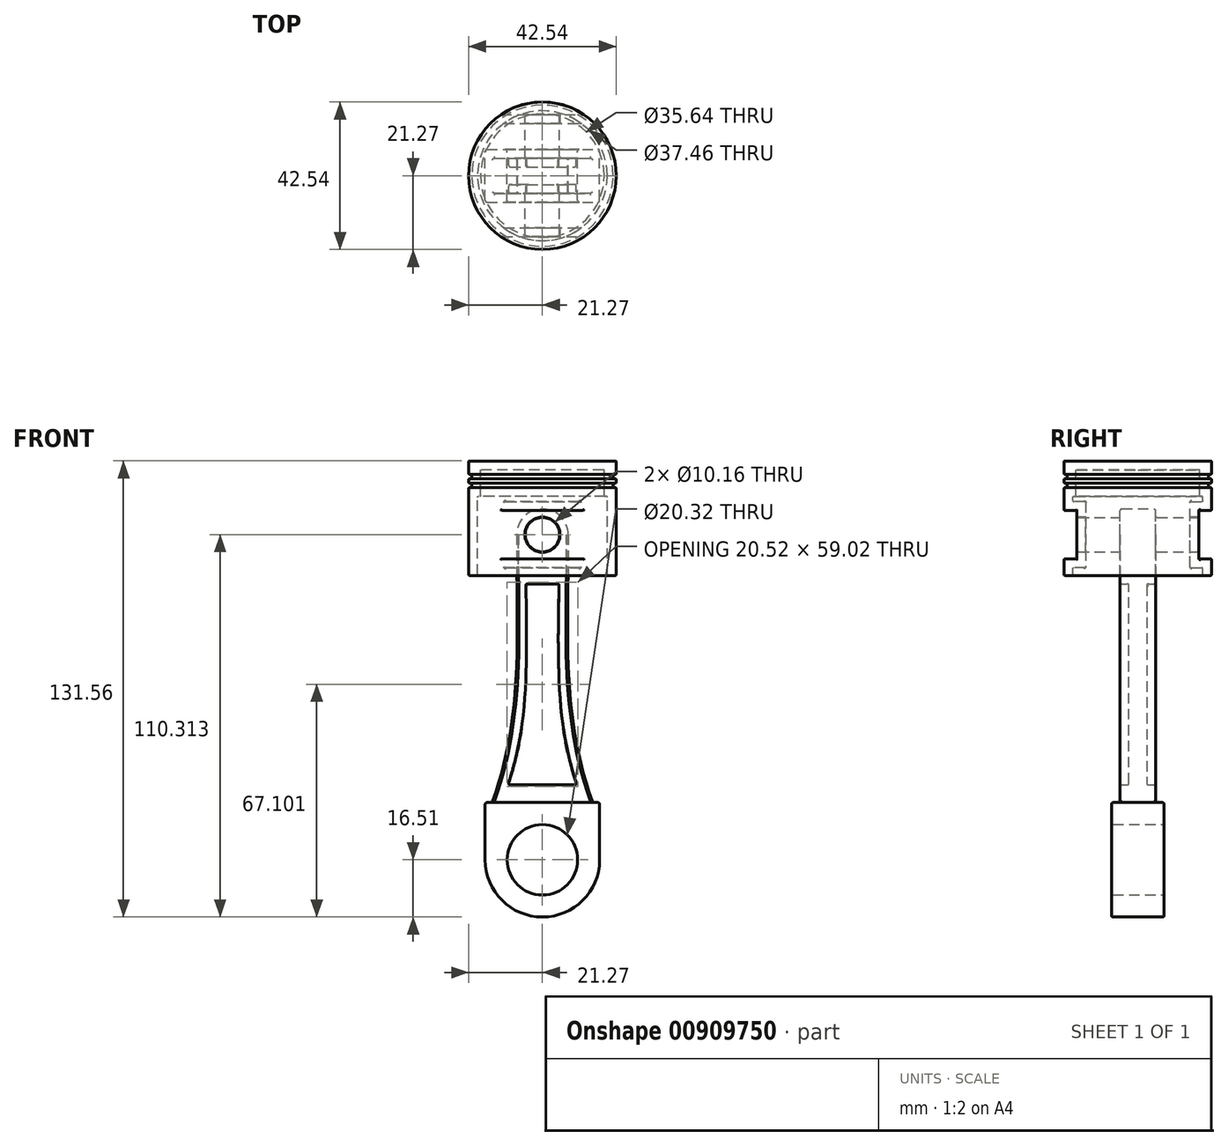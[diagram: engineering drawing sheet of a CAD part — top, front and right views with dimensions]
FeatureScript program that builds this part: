
annotation { "Feature Type Name" : "Feature", "Feature Type Description" : "" }
export const myFeature = defineFeature(function(context is Context, id is Id, definition is map)
    precondition{}
    {
        {
            var Q0;
            Q0=qCreatedBy(makeId("Front.planeOp"),FACE);
            var sketch = newSketch(context, id + "F0", { "sketchPlane" : qUnion([Q0])});
            skLineSegment(sketch, "E0", {"start": v(-248.97, 187.24) * mm, "end": v(-248.97, -66.76) * mm});
            skLineSegment(sketch, "E1", {"start": v(221.96, 188.73) * mm, "end": v(289.05, 188.73) * mm});
            skSolve(sketch);
        }
        {
            var Q0;
            Q0=qCreatedBy(makeId("Front.planeOp"),FACE);
            var sketch = newSketch(context, id + "F1", { "sketchPlane" : qUnion([Q0])});
            skLineSegment(sketch, "E2.bottom", {"start": v(0, 115.05) * mm, "end": v(21.27, 115.05) * mm});
            skLineSegment(sketch, "E2.top", {"start": v(0, 82.03) * mm, "end": v(21.27, 82.03) * mm});
            skLineSegment(sketch, "E2.left", {"start": v(0, 115.05) * mm, "end": v(0, 111.17) * mm});
            skLineSegment(sketch, "E2.right", {"start": v(21.27, 115.05) * mm, "end": v(21.27, 111.17) * mm});
            skLineSegment(sketch, "E3.left", {"start": v(0, 111.17) * mm, "end": v(0, 109.9) * mm});
            skLineSegment(sketch, "E3.right", {"start": v(20.36, 111.17) * mm, "end": v(20.36, 109.9) * mm});
            skLineSegment(sketch, "E4.left", {"start": v(20.36, 108.63) * mm, "end": v(20.36, 107.36) * mm});
            skLineSegment(sketch, "E4.right", {"start": v(0, 108.63) * mm, "end": v(0, 107.36) * mm});
            skLineSegment(sketch, "E5", {"start": v(20.36, 111.17) * mm, "end": v(21.27, 111.17) * mm});
            skLineSegment(sketch, "E6", {"start": v(20.36, 109.9) * mm, "end": v(21.27, 109.9) * mm});
            skLineSegment(sketch, "E7", {"start": v(20.36, 108.63) * mm, "end": v(21.27, 108.63) * mm});
            skLineSegment(sketch, "E8", {"start": v(20.36, 107.36) * mm, "end": v(21.27, 107.36) * mm});
            skLineSegment(sketch, "E9.trimOffspring", {"start": v(21.27, 107.36) * mm, "end": v(21.27, 82.03) * mm});
            skLineSegment(sketch, "E10.trimOffspring", {"start": v(21.27, 109.9) * mm, "end": v(21.27, 108.63) * mm});
            skLineSegment(sketch, "E11.trimOffspring", {"start": v(0, 109.9) * mm, "end": v(0, 108.63) * mm});
            skLineSegment(sketch, "E12.trimOffspring", {"start": v(0, 107.36) * mm, "end": v(0, 82.03) * mm});
            skSolve(sketch);
        }
        {
            var Q0;
            Q0 = qSketchRegion(id + "F1", true);
            var Q1;
            Q1=sQuery(id+"F1.wireOp",EDGE,"E12.trimOffspring");
            revolve(context, id + "F2", {"surfaceOperationType" : NewSurfaceOperationType.NEW, "entities" : qUnion([Q0]), "axis" : qUnion([Q1]), "revolveType" : RevolveType.FULL});
        }
        {
            var Q0;
            Q0=qCreatedBy(makeId("Right.planeOp"),FACE);
            var sketch = newSketch(context, id + "F3", { "sketchPlane" : qUnion([Q0])});
            skLineSegment(sketch, "E13.bottom", {"start": v(-21.43, 100.81) * mm, "end": v(-17.58, 100.81) * mm});
            skLineSegment(sketch, "E13.top", {"start": v(-21.43, 86.8) * mm, "end": v(-17.58, 86.8) * mm});
            skLineSegment(sketch, "E13.left", {"start": v(-21.43, 100.81) * mm, "end": v(-21.43, 86.8) * mm});
            skLineSegment(sketch, "E13.right", {"start": v(-17.58, 100.81) * mm, "end": v(-17.58, 86.8) * mm});
            skLineSegment(sketch, "E14.MirrorCS", {"start": v(17.58, 100.81) * mm, "end": v(17.58, 86.8) * mm});
            skLineSegment(sketch, "E15.MirrorCS", {"start": v(21.43, 100.81) * mm, "end": v(17.58, 100.81) * mm});
            skLineSegment(sketch, "E16.MirrorCS", {"start": v(21.43, 86.8) * mm, "end": v(17.58, 86.8) * mm});
            skLineSegment(sketch, "E17.MirrorCS", {"start": v(21.43, 100.81) * mm, "end": v(21.43, 86.8) * mm});
            skSolve(sketch);
        }
        {
            var Q0;
            Q0 = qSketchRegion(id + "F3", true);
            extrude(context, id + "F4", {"entities" : qUnion([Q0]), "operationType" : NewBodyOperationType.REMOVE, "oppositeDirection" : true, "depth" : 30.23 * mm, "offsetDistance" : 25.4 * mm, "hasSecondDirection" : true, "secondDirectionOppositeDirection" : false, "secondDirectionDepth" : 46.23 * mm});
        }
        {
            var Q0;
            Q0=makeQuery(id+"F2.opRevolve","SWEPT_FACE",FACE,{"disambiguationData":[OSD([sQuery(id+"F1.wireOp",EDGE,"E2.top")])]});
            shell(context, id + "F5", {"entities" : qUnion([Q0]), "thickness" : 2.54 * mm});
        }
        {
            var Q0;
            Q0=qCreatedBy(makeId("Front.planeOp"),FACE);
            var sketch = newSketch(context, id + "F6", { "sketchPlane" : qUnion([Q0])});
            skCircle(sketch, "E18", {"center": v(0, 93.8) * mm, "radius": 5.08 * mm});
            skSolve(sketch);
        }
        {
            var Q0;
            Q0 = qSketchRegion(id + "F6", true);
            extrude(context, id + "F7", {"entities" : qUnion([Q0]), "operationType" : NewBodyOperationType.REMOVE, "oppositeDirection" : true, "depth" : 25.4 * mm, "offsetDistance" : 25.4 * mm, "hasSecondDirection" : true, "secondDirectionOppositeDirection" : false, "secondDirectionDepth" : 25.4 * mm});
        }
        {
            var Q0;
            Q0=qCreatedBy(makeId("Front.planeOp"),FACE);
            var sketch = newSketch(context, id + "F8", { "sketchPlane" : qUnion([Q0])});
            skCircle(sketch, "E19", {"center": v(0, 0) * mm, "radius": 10.16 * mm});
            skArc(sketch, "E20", {"start": v(-16.51, 0) * mm, "mid": v(0, -16.51) * mm, "end": v(16.51, 0) * mm});
            skLineSegment(sketch, "E21.bottom", {"start": v(-16.51, 0) * mm, "end": v(16.51, 0) * mm});
            skLineSegment(sketch, "E21.top", {"start": v(-16.51, 16.51) * mm, "end": v(16.51, 16.51) * mm});
            skLineSegment(sketch, "E21.left", {"start": v(-16.51, 0) * mm, "end": v(-16.51, 16.51) * mm});
            skLineSegment(sketch, "E21.right", {"start": v(16.51, 0) * mm, "end": v(16.51, 16.51) * mm});
            skSolve(sketch);
        }
        {
            var Q0;
            Q0 = qSketchRegion(id + "F8", true);
            extrude(context, id + "F9", {"entities" : qUnion([Q0]), "depth" : 7.62 * mm, "offsetDistance" : 25.4 * mm, "hasSecondDirection" : true, "secondDirectionOppositeDirection" : true, "secondDirectionDepth" : 7.62 * mm});
        }
        {
            var Q0;
            Q0=qCreatedBy(makeId("Front.planeOp"),FACE);
            var sketch = newSketch(context, id + "F10", { "sketchPlane" : qUnion([Q0])});
            skFitSpline(sketch, "E22", {"points": [v(7.42, 93.84) * mm, v(14.48, 16.51) * mm], "startDerivative": vector(0.4, -85.18) * mm, "endDerivative": vector(27.69, -77.4) * mm});
            skLineSegment(sketch, "E23", {"start": v(0, 0) * mm, "end": v(0, 21.54) * mm});
            skFitSpline(sketch, "E24.MirrorCS", {"points": [v(-7.42, 93.84) * mm, v(-14.48, 16.51) * mm], "startDerivative": vector(-0.4, -85.18) * mm, "endDerivative": vector(-27.69, -77.4) * mm});
            skArc(sketch, "E25", {"start": v(-7.42, 93.84) * mm, "mid": v(0, 101.22) * mm, "end": v(7.42, 93.84) * mm});
            skFitSpline(sketch, "E26.0", {"points": [v(-4.88, 93.83) * mm, v(-4.91, 86.76) * mm, v(-4.68, 73.25) * mm, v(-4.71, 54.03) * mm, v(-6.49, 35.11) * mm, v(-9.73, 22.25) * mm, v(-12.1, 15.65) * mm]});
            skFitSpline(sketch, "E26.2", {"points": [v(4.88, 93.83) * mm, v(4.91, 86.76) * mm, v(4.68, 73.25) * mm, v(4.71, 54.03) * mm, v(6.49, 35.11) * mm, v(9.73, 22.25) * mm, v(12.1, 15.65) * mm]});
            skLineSegment(sketch, "E27", {"start": v(-4.8, 79.6) * mm, "end": v(4.8, 79.6) * mm});
            skLineSegment(sketch, "E28.trimOffspring", {"start": v(-10.15, 21.59) * mm, "end": v(10.15, 21.59) * mm});
            skLineSegment(sketch, "E29", {"start": v(-14.48, 16.51) * mm, "end": v(14.48, 16.51) * mm});
            skSolve(sketch);
        }
        {
            var Q0;
            Q0 = qSketchRegion(id + "F10", true);
            extrude(context, id + "F11", {"entities" : qUnion([Q0]), "operationType" : NewBodyOperationType.ADD, "depth" : 5.08 * mm, "offsetDistance" : 25.4 * mm, "hasSecondDirection" : true, "secondDirectionOppositeDirection" : true, "secondDirectionDepth" : 5.08 * mm});
        }
        {
            var Q0;
            Q0=qCreatedBy(makeId("Front.planeOp"),FACE);
            var sketch = newSketch(context, id + "F12", { "sketchPlane" : qUnion([Q0])});
            skLineSegment(sketch, "E30.0", {"start": v(-4.8, 79.6) * mm, "end": v(4.8, 79.6) * mm});
            skFitSpline(sketch, "E31.0", {"points": [v(-4.88, 93.83) * mm, v(-4.91, 86.76) * mm, v(-4.68, 73.25) * mm, v(-4.71, 54.03) * mm, v(-6.49, 35.11) * mm, v(-9.73, 22.25) * mm, v(-12.1, 15.65) * mm]});
            skLineSegment(sketch, "E32.0", {"start": v(-10.15, 21.59) * mm, "end": v(10.15, 21.59) * mm});
            skFitSpline(sketch, "E33.0", {"points": [v(4.88, 93.83) * mm, v(4.91, 86.76) * mm, v(4.68, 73.25) * mm, v(4.71, 54.03) * mm, v(6.49, 35.11) * mm, v(9.73, 22.25) * mm, v(12.1, 15.65) * mm]});
            skSolve(sketch);
        }
        {
            var Q0;
            Q0 = qSketchRegion(id + "F12", true);
            extrude(context, id + "F13", {"entities" : qUnion([Q0]), "operationType" : NewBodyOperationType.ADD, "depth" : 2.54 * mm, "offsetDistance" : 25.4 * mm, "hasSecondDirection" : true, "secondDirectionOppositeDirection" : true, "secondDirectionDepth" : 2.54 * mm});
        }
        {
            var Q0;
            Q0=qCreatedBy(makeId("Front.planeOp"),FACE);
            var sketch = newSketch(context, id + "F14", { "sketchPlane" : qUnion([Q0])});
            skCircle(sketch, "E34.0", {"center": v(0, 93.8) * mm, "radius": 4.95 * mm});
            skSolve(sketch);
        }
        {
            var Q0;
            Q0 = qSketchRegion(id + "F14", true);
            var Q1;
            Q1=makeQuery(id+"F4.boolean.opBoolean","COPY",FACE,{"derivedFrom":makeQuery(id+"F4.opExtrude","SWEPT_FACE",FACE,{"disambiguationData":[OSD([sQuery(id+"F3.wireOp",EDGE,"E13.right")])]})});
            var Q2;
            Q2=makeQuery(id+"F4.boolean.opBoolean","COPY",FACE,{"derivedFrom":makeQuery(id+"F4.opExtrude","SWEPT_FACE",FACE,{"disambiguationData":[OSD([sQuery(id+"F3.wireOp",EDGE,"E14.MirrorCS")])]})});
            extrude(context, id + "F15", {"entities" : qUnion([Q0]), "operationType" : NewBodyOperationType.ADD, "endBound" : BoundingType.UP_TO_SURFACE, "depth" : 25.4 * mm, "endBoundEntityFace" : qUnion([Q1]), "offsetDistance" : 25.4 * mm, "hasSecondDirection" : true, "secondDirectionBound" : SecondDirectionBoundingType.UP_TO_SURFACE, "secondDirectionOppositeDirection" : true, "secondDirectionDepth" : 25.4 * mm, "secondDirectionBoundEntityFace" : qUnion([Q2])});
        }
        {
            var Q0;
            Q0=makeQuery(id+"F9.opExtrude","CAP_FACE",FACE,{"disambiguationData":[OSD([sQuery(id+"F8.wireOp",EDGE,"E19"),sQuery(id+"F8.wireOp",EDGE,"E20"),sQuery(id+"F8.wireOp",EDGE,"E21.top"),sQuery(id+"F8.wireOp",EDGE,"E21.left"),sQuery(id+"F8.wireOp",EDGE,"E21.right")])],"isStart":false});
            var Q1;
            Q1=makeQuery(id+"F11.opExtrude","CAP_EDGE",EDGE,{"disambiguationData":[OSD([sQuery(id+"F10.wireOp",EDGE,"E29")])],"isStart":true});
            var Q2;
            Q2=makeQuery(id+"F9.opExtrude","SWEPT_FACE",FACE,{"disambiguationData":[OSD([sQuery(id+"F8.wireOp",EDGE,"E21.top")])]});
            var Q3;
            Q3=makeQuery(id+"F9.opExtrude","SWEPT_FACE",FACE,{"disambiguationData":[OSD([sQuery(id+"F8.wireOp",EDGE,"E19")])]});
            var Q4;
            Q4=makeQuery(id+"F9.opExtrude","CAP_FACE",FACE,{"disambiguationData":[OSD([sQuery(id+"F8.wireOp",EDGE,"E19"),sQuery(id+"F8.wireOp",EDGE,"E20"),sQuery(id+"F8.wireOp",EDGE,"E21.top"),sQuery(id+"F8.wireOp",EDGE,"E21.left"),sQuery(id+"F8.wireOp",EDGE,"E21.right")])],"isStart":true});
            var Q5;
            Q5=makeQuery(id+"F13.opExtrude","CAP_FACE",FACE,{"disambiguationData":[OSD([sQuery(id+"F12.wireOp",EDGE,"E30.0"),sQuery(id+"F12.wireOp",EDGE,"E31.0"),sQuery(id+"F12.wireOp",EDGE,"E32.0"),sQuery(id+"F12.wireOp",EDGE,"E33.0")])],"isStart":true});
            var Q6;
            Q6=makeQuery(id+"F11.opExtrude","SWEPT_FACE",FACE,{"disambiguationData":[OSD([sQuery(id+"F10.wireOp",EDGE,"E24.MirrorCS")])]});
            var Q7;
            Q7=makeQuery(id+"F11.opExtrude","CAP_FACE",FACE,{"disambiguationData":[OSD([sQuery(id+"F10.wireOp",EDGE,"E22"),sQuery(id+"F10.wireOp",EDGE,"E24.MirrorCS"),sQuery(id+"F10.wireOp",EDGE,"E25"),sQuery(id+"F10.wireOp",EDGE,"E26.0"),sQuery(id+"F10.wireOp",EDGE,"E26.2"),sQuery(id+"F10.wireOp",EDGE,"E27"),sQuery(id+"F10.wireOp",EDGE,"E28.trimOffspring"),sQuery(id+"F10.wireOp",EDGE,"E29")])],"isStart":true});
            var Q8;
            Q8=makeQuery(id+"F11.opExtrude","CAP_FACE",FACE,{"disambiguationData":[OSD([sQuery(id+"F10.wireOp",EDGE,"E22"),sQuery(id+"F10.wireOp",EDGE,"E24.MirrorCS"),sQuery(id+"F10.wireOp",EDGE,"E25"),sQuery(id+"F10.wireOp",EDGE,"E26.0"),sQuery(id+"F10.wireOp",EDGE,"E26.2"),sQuery(id+"F10.wireOp",EDGE,"E27"),sQuery(id+"F10.wireOp",EDGE,"E28.trimOffspring"),sQuery(id+"F10.wireOp",EDGE,"E29")])],"isStart":false});
            var Q9;
            Q9=makeQuery(id+"F13.opExtrude","CAP_FACE",FACE,{"disambiguationData":[OSD([sQuery(id+"F12.wireOp",EDGE,"E30.0"),sQuery(id+"F12.wireOp",EDGE,"E31.0"),sQuery(id+"F12.wireOp",EDGE,"E32.0"),sQuery(id+"F12.wireOp",EDGE,"E33.0")])],"isStart":false});
            var Q10;
            {var subQ2=sQuery(id+"F10.wireOp",EDGE,"E26.2");Q10=makeQuery(id+"F13.boolean.opBoolean","SPLIT",FACE,{"disambiguationData":[TD([makeQuery(id+"F13.opExtrude","CAP_FACE",FACE,{"disambiguationData":[OSD([sQuery(id+"F12.wireOp",EDGE,"E30.0"),sQuery(id+"F12.wireOp",EDGE,"E31.0"),sQuery(id+"F12.wireOp",EDGE,"E32.0"),sQuery(id+"F12.wireOp",EDGE,"E33.0")])],"isStart":false})])],"derivedFrom":makeQuery(id+"F11.opExtrude","SWEPT_FACE",FACE,{"disambiguationData":[OSD([subQ2])]})});}
            var Q11;
            {var subQ2=sQuery(id+"F10.wireOp",EDGE,"E26.0");Q11=makeQuery(id+"F13.boolean.opBoolean","SPLIT",FACE,{"disambiguationData":[TD([makeQuery(id+"F13.opExtrude","CAP_FACE",FACE,{"disambiguationData":[OSD([sQuery(id+"F12.wireOp",EDGE,"E30.0"),sQuery(id+"F12.wireOp",EDGE,"E31.0"),sQuery(id+"F12.wireOp",EDGE,"E32.0"),sQuery(id+"F12.wireOp",EDGE,"E33.0")])],"isStart":false})])],"derivedFrom":makeQuery(id+"F11.opExtrude","SWEPT_FACE",FACE,{"disambiguationData":[OSD([subQ2])]})});}
            var Q12;
            {var subQ0=sQuery(id+"F10.wireOp",EDGE,"E28.trimOffspring");Q12=makeQuery(id+"F13.boolean.opBoolean","SPLIT",FACE,{"disambiguationData":[TD([makeQuery(id+"F13.opExtrude","CAP_FACE",FACE,{"disambiguationData":[OSD([sQuery(id+"F12.wireOp",EDGE,"E30.0"),sQuery(id+"F12.wireOp",EDGE,"E31.0"),sQuery(id+"F12.wireOp",EDGE,"E32.0"),sQuery(id+"F12.wireOp",EDGE,"E33.0")])],"isStart":true})])],"derivedFrom":makeQuery(id+"F11.opExtrude","SWEPT_FACE",FACE,{"disambiguationData":[OSD([subQ0])]})});}
            var Q13;
            {var subQ0=sQuery(id+"F10.wireOp",EDGE,"E27");Q13=makeQuery(id+"F13.boolean.opBoolean","SPLIT",FACE,{"disambiguationData":[TD([makeQuery(id+"F13.opExtrude","CAP_FACE",FACE,{"disambiguationData":[OSD([sQuery(id+"F12.wireOp",EDGE,"E30.0"),sQuery(id+"F12.wireOp",EDGE,"E31.0"),sQuery(id+"F12.wireOp",EDGE,"E32.0"),sQuery(id+"F12.wireOp",EDGE,"E33.0")])],"isStart":true})])],"derivedFrom":makeQuery(id+"F11.opExtrude","SWEPT_FACE",FACE,{"disambiguationData":[OSD([subQ0])]})});}
            var Q14;
            {var subQ0=sQuery(id+"F14.wireOp",EDGE,"E34.0");Q14=makeQuery(id+"F15.boolean.opBoolean","SPLIT",FACE,{"disambiguationData":[TD([makeQuery(id+"F15.opExtrude","CAP_FACE",FACE,{"disambiguationData":[OSD([subQ0])],"isStart":true})])],"derivedFrom":makeQuery(id+"F15.opExtrude","SWEPT_FACE",FACE,{"disambiguationData":[OSD([subQ0])]})});}
            var Q15;
            {var subQ0=sQuery(id+"F14.wireOp",EDGE,"E34.0");Q15=makeQuery(id+"F15.boolean.opBoolean","SPLIT",FACE,{"disambiguationData":[TD([makeQuery(id+"F15.opExtrude","CAP_FACE",FACE,{"disambiguationData":[OSD([subQ0])],"isStart":false})])],"derivedFrom":makeQuery(id+"F15.opExtrude","SWEPT_FACE",FACE,{"disambiguationData":[OSD([subQ0])]})});}
            fillet(context, id + "F16", {"entities" : qUnion([Q0, Q1, Q2, Q3, Q4, Q5, Q6, Q7, Q8, Q9, Q10, Q11, Q12, Q13, Q14, Q15]), "radius" : 0.5 * mm, "tangentPropagation" : true, "allowEdgeOverflow" : false});
        }
        {
            var Q0;
            Q0=makeQuery(id+"F2.opRevolve","SWEPT_FACE",FACE,{"disambiguationData":[OSD([sQuery(id+"F1.wireOp",EDGE,"E2.bottom")])]});
            var Q1;
            Q1=makeQuery(id+"F2.opRevolve","SWEPT_FACE",FACE,{"disambiguationData":[OSD([sQuery(id+"F1.wireOp",EDGE,"E9.trimOffspring")])]});
            var Q2;
            Q2=makeQuery(id+"F4.boolean.opBoolean","COPY",FACE,{"derivedFrom":makeQuery(id+"F4.opExtrude","SWEPT_FACE",FACE,{"disambiguationData":[OSD([sQuery(id+"F3.wireOp",EDGE,"E14.MirrorCS")])]})});
            var Q3;
            Q3=makeQuery(id+"F2.opRevolve","SWEPT_EDGE",EDGE,{"disambiguationData":[OSD([sQuery(id+"F1.wireOp",EDGE,"E3.right"),sQuery(id+"F1.wireOp",EDGE,"E6")])]});
            var Q4;
            Q4=makeQuery(id+"F2.opRevolve","SWEPT_FACE",FACE,{"disambiguationData":[OSD([sQuery(id+"F1.wireOp",EDGE,"E2.right")])]});
            var Q5;
            Q5=makeQuery(id+"F2.opRevolve","SWEPT_FACE",FACE,{"disambiguationData":[OSD([sQuery(id+"F1.wireOp",EDGE,"E3.right")])]});
            var Q6;
            Q6=makeQuery(id+"F2.opRevolve","SWEPT_FACE",FACE,{"disambiguationData":[OSD([sQuery(id+"F1.wireOp",EDGE,"E4.left")])]});
            var Q7;
            Q7=makeQuery(id+"F2.opRevolve","SWEPT_FACE",FACE,{"disambiguationData":[OSD([sQuery(id+"F1.wireOp",EDGE,"E8")])]});
            var Q8;
            Q8=makeQuery(id+"F2.opRevolve","SWEPT_FACE",FACE,{"disambiguationData":[OSD([sQuery(id+"F1.wireOp",EDGE,"E10.trimOffspring")])]});
            var Q9;
            Q9=makeQuery(id+"F5.opShell","OFFSET_FACE",FACE,{"disambiguationData":[OSD([sQuery(id+"F1.wireOp",EDGE,"E9.trimOffspring")])]});
            var Q10;
            Q10=makeQuery(id+"F5.opShell","OFFSET_FACE",FACE,{"disambiguationData":[OSD([sQuery(id+"F3.wireOp",EDGE,"E13.right")])]});
            var Q11;
            Q11=makeQuery(id+"F5.opShell","OFFSET_FACE",FACE,{"disambiguationData":[OSD([sQuery(id+"F3.wireOp",EDGE,"E14.MirrorCS")])]});
            var Q12;
            Q12=makeQuery(id+"F5.opShell","OFFSET_FACE",FACE,{"disambiguationData":[OSD([sQuery(id+"F1.wireOp",EDGE,"E2.bottom")])]});
            var Q13;
            Q13=makeQuery(id+"F5.opShell","OFFSET_FACE",FACE,{"disambiguationData":[OSD([sQuery(id+"F1.wireOp",EDGE,"E8")])]});
            fillet(context, id + "F17", {"entities" : qUnion([Q0, Q1, Q2, Q3, Q4, Q5, Q6, Q7, Q8, Q9, Q10, Q11, Q12, Q13]), "radius" : 0.25 * mm, "tangentPropagation" : true, "allowEdgeOverflow" : false});
        }
    });
